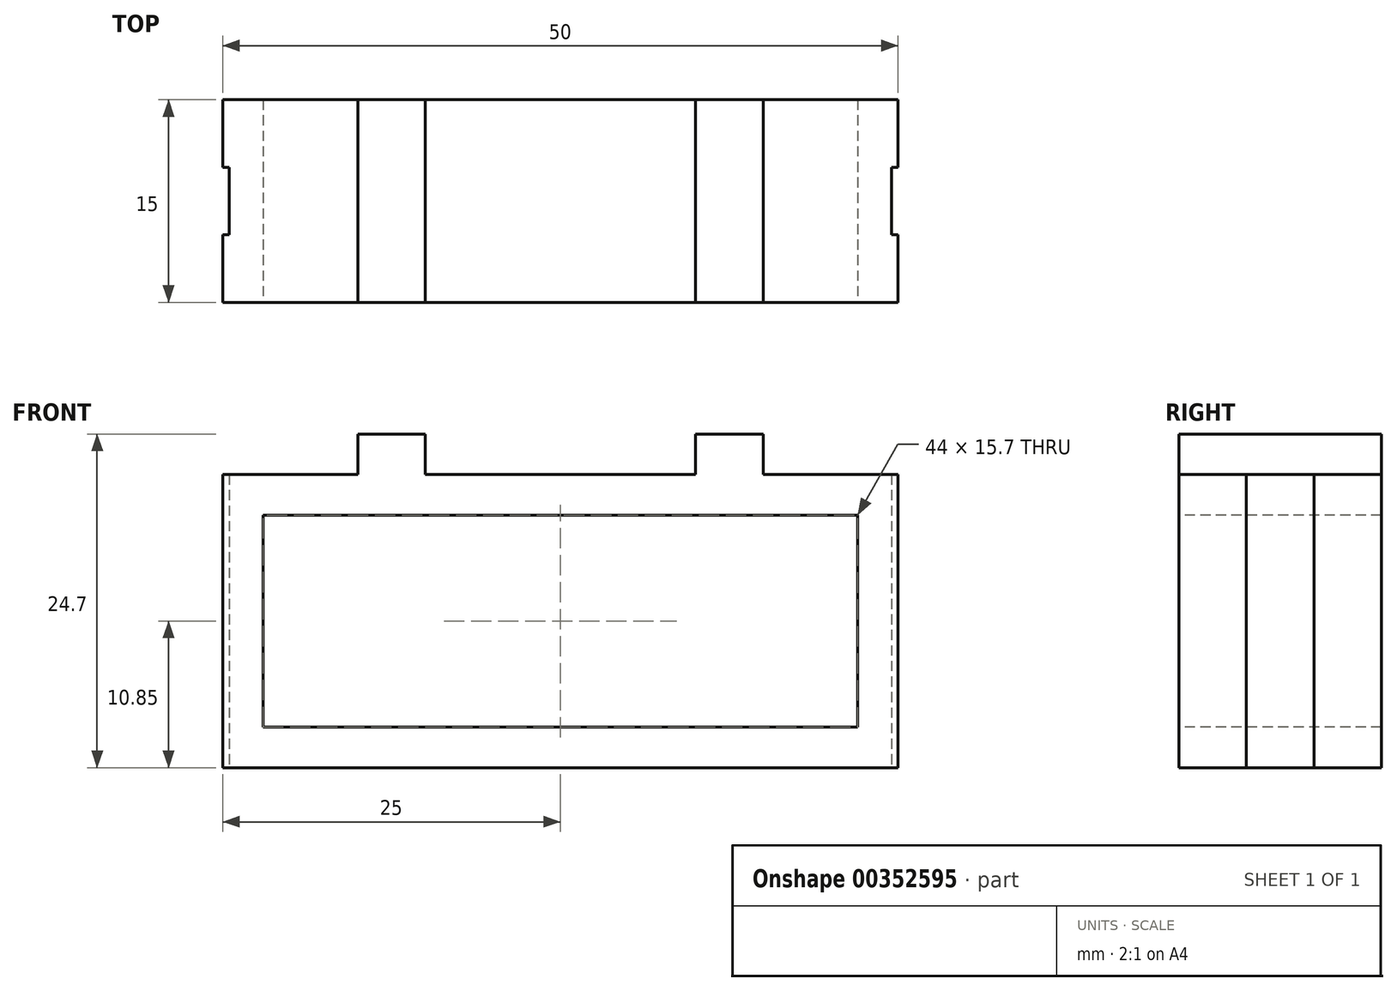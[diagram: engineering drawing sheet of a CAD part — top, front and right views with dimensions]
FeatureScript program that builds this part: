
annotation { "Feature Type Name" : "Feature", "Feature Type Description" : "" }
export const myFeature = defineFeature(function(context is Context, id is Id, definition is map)
    precondition{}
    {
        {
            var Q0;
            Q0=qCreatedBy(makeId("Front.planeOp"),FACE);
            var sketch = newSketch(context, id + "F0", { "sketchPlane" : qUnion([Q0])});
            skLineSegment(sketch, "E0.bottom", {"start": v(-25, 10.85) * mm, "end": v(-15, 10.85) * mm});
            skLineSegment(sketch, "E0.top", {"start": v(-25, -10.85) * mm, "end": v(25, -10.85) * mm});
            skLineSegment(sketch, "E0.left", {"start": v(-25, 10.85) * mm, "end": v(-25, -10.85) * mm});
            skLineSegment(sketch, "E0.right", {"start": v(25, 10.85) * mm, "end": v(25, -10.85) * mm});
            skLineSegment(sketch, "E1.top", {"start": v(-10, 13.85) * mm, "end": v(-15, 13.85) * mm});
            skLineSegment(sketch, "E1.left", {"start": v(-10, 10.85) * mm, "end": v(-10, 13.85) * mm});
            skLineSegment(sketch, "E1.right", {"start": v(-15, 10.85) * mm, "end": v(-15, 13.85) * mm});
            skLineSegment(sketch, "E2.top", {"start": v(10, 13.85) * mm, "end": v(15, 13.85) * mm});
            skLineSegment(sketch, "E2.left", {"start": v(10, 10.85) * mm, "end": v(10, 13.85) * mm});
            skLineSegment(sketch, "E2.right", {"start": v(15, 10.85) * mm, "end": v(15, 13.85) * mm});
            skLineSegment(sketch, "E3.bottom", {"start": v(22, -7.85) * mm, "end": v(-22, -7.85) * mm});
            skLineSegment(sketch, "E3.top", {"start": v(22, 7.85) * mm, "end": v(-22, 7.85) * mm});
            skLineSegment(sketch, "E3.left", {"start": v(22, -7.85) * mm, "end": v(22, 7.85) * mm});
            skLineSegment(sketch, "E3.right", {"start": v(-22, -7.85) * mm, "end": v(-22, 7.85) * mm});
            skLineSegment(sketch, "E4.trimOffspring", {"start": v(-10, 10.85) * mm, "end": v(10, 10.85) * mm});
            skLineSegment(sketch, "E5.trimOffspring", {"start": v(15, 10.85) * mm, "end": v(25, 10.85) * mm});
            skSolve(sketch);
        }
        {
            var Q0;
            Q0=makeQuery(id+"F0.imprint","IMPRINT",FACE,{"disambiguationData":[TD([[makeQuery(id+"F0.imprint","IMPRINT",EDGE,{"derivedFrom":sQuery(id+"F0.wireOp",EDGE,"E0.bottom")}),-1.0]])]});
            extrude(context, id + "F1", {"entities" : qUnion([Q0]), "oppositeDirection" : true, "depth" : 15 * mm});
        }
        {
            var Q0;
            Q0=makeQuery(id+"F1.opExtrude","SWEPT_FACE",FACE,{"disambiguationData":[OSD([sQuery(id+"F0.wireOp",EDGE,"E0.top")])]});
            var sketch = newSketch(context, id + "F2", { "sketchPlane" : qUnion([Q0])});
            skLineSegment(sketch, "E6.bottom", {"start": v(-25, -5) * mm, "end": v(-24.5, -5) * mm});
            skLineSegment(sketch, "E6.top", {"start": v(-25, -10) * mm, "end": v(-24.5, -10) * mm});
            skLineSegment(sketch, "E6.left", {"start": v(-25, -5) * mm, "end": v(-25, -10) * mm});
            skLineSegment(sketch, "E6.right", {"start": v(-24.5, -5) * mm, "end": v(-24.5, -10) * mm});
            skLineSegment(sketch, "E7.MirrorCS", {"start": v(24.5, -5) * mm, "end": v(24.5, -10) * mm});
            skLineSegment(sketch, "E8.MirrorCS", {"start": v(25, -5) * mm, "end": v(24.5, -5) * mm});
            skLineSegment(sketch, "E9.MirrorCS", {"start": v(25, -10) * mm, "end": v(24.5, -10) * mm});
            skLineSegment(sketch, "E10.MirrorCS", {"start": v(25, -5) * mm, "end": v(25, -10) * mm});
            skSolve(sketch);
        }
        {
            var Q0;
            Q0 = qSketchRegion(id + "F2", true);
            extrude(context, id + "F3", {"entities" : qUnion([Q0]), "operationType" : NewBodyOperationType.REMOVE, "oppositeDirection" : true, "depth" : 25 * mm});
        }
    });
